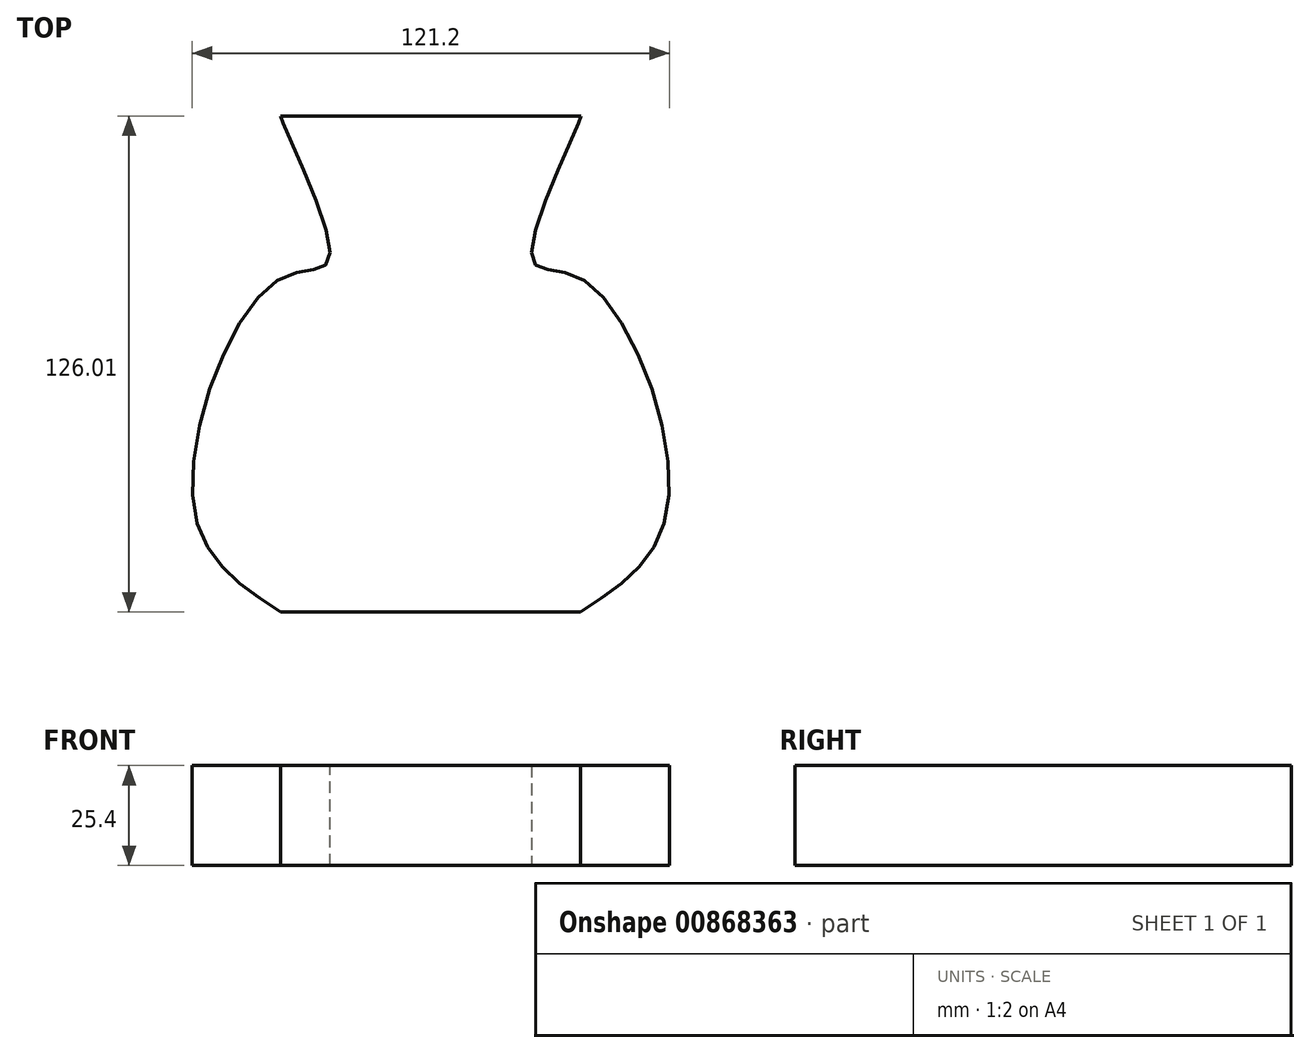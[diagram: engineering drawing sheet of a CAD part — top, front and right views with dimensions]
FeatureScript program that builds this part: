
annotation { "Feature Type Name" : "Feature", "Feature Type Description" : "" }
export const myFeature = defineFeature(function(context is Context, id is Id, definition is map)
    precondition{}
    {
        {
            var Q0;
            Q0=qCreatedBy(makeId("Top.planeOp"),FACE);
            var sketch = newSketch(context, id + "F0", { "sketchPlane" : qUnion([Q0])});
            skLineSegment(sketch, "E0", {"start": v(0, -71.52) * mm, "end": v(-38.1, -71.52) * mm});
            skLineSegment(sketch, "E1", {"start": v(0, -71.52) * mm, "end": v(38.1, -71.52) * mm});
            skFitSpline(sketch, "E2", {"points": [v(-38.1, -71.52) * mm, v(-60.29, -44.28) * mm, v(-38.1, 13.28) * mm, v(-25.66, 18.52) * mm, v(-38.1, 54.15) * mm, v(-38.1, 54.55) * mm], "startDerivative": vector(-124.79, 80.47) * mm, "endDerivative": vector(4.92, 6.12) * mm});
            skFitSpline(sketch, "E3.MirrorCS", {"points": [v(38.1, -71.52) * mm, v(60.29, -44.28) * mm, v(38.1, 13.28) * mm, v(25.66, 18.52) * mm, v(38.1, 54.15) * mm, v(38.1, 54.55) * mm], "startDerivative": vector(124.79, 80.47) * mm, "endDerivative": vector(-4.92, 6.12) * mm});
            skLineSegment(sketch, "E4", {"start": v(-38.14, 54.5) * mm, "end": v(38.14, 54.5) * mm});
            skSolve(sketch);
        }
        {
            var Q0;
            {var subQ5=sQuery(id+"F0.wireOp",EDGE,"E0");Q0=makeQuery(id+"F0.imprint","IMPRINT",FACE,{"disambiguationData":[TD([[makeQuery(id+"F0.imprint","IMPRINT",EDGE,{"derivedFrom":subQ5}),-1.0]])]});}
            extrude(context, id + "F1", {"entities" : qUnion([Q0]), "depth" : 25.4 * mm, "offsetDistance" : 25.4 * mm});
        }
    });
